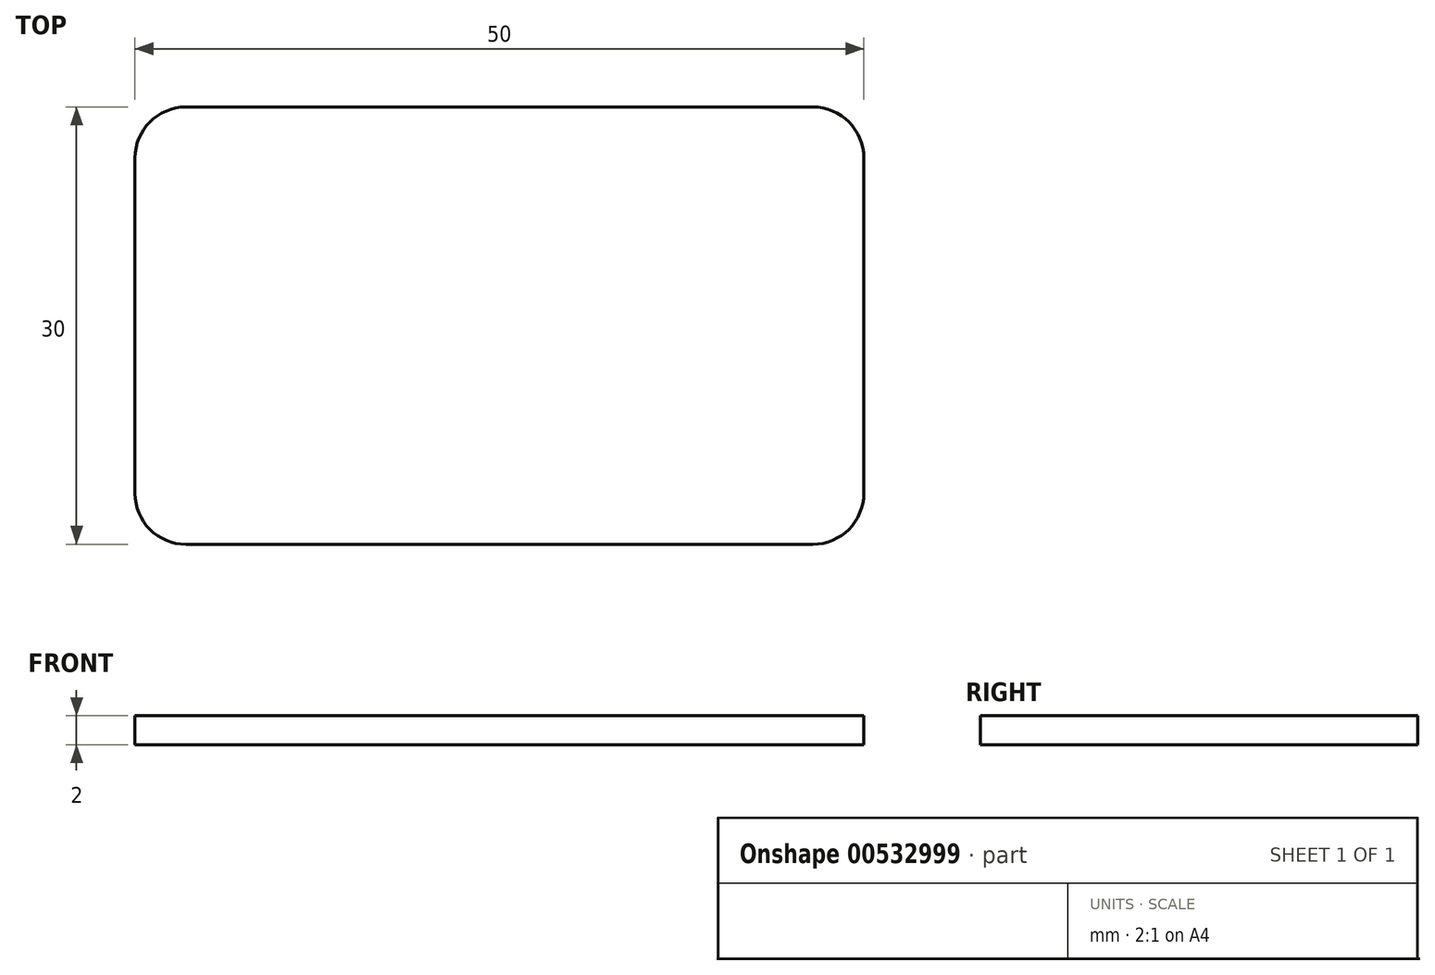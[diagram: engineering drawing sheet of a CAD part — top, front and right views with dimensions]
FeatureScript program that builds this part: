
annotation { "Feature Type Name" : "Feature", "Feature Type Description" : "" }
export const myFeature = defineFeature(function(context is Context, id is Id, definition is map)
    precondition{}
    {
        {
            var Q0;
            Q0=qCreatedBy(makeId("Top.planeOp"),FACE);
            var sketch = newSketch(context, id + "F0", { "sketchPlane" : qUnion([Q0])});
            skLineSegment(sketch, "E0.bottom", {"start": v(21.5, 15) * mm, "end": v(-21.5, 15) * mm});
            skLineSegment(sketch, "E0.top", {"start": v(21.5, -15) * mm, "end": v(-21.5, -15) * mm});
            skLineSegment(sketch, "E0.left", {"start": v(25, 11.5) * mm, "end": v(25, -11.5) * mm});
            skLineSegment(sketch, "E0.right", {"start": v(-25, 11.5) * mm, "end": v(-25, -11.5) * mm});
            skPoint(sketch, "E0.middle", {"position": v(0, 0) * mm});
            skPoint(sketch, "E1.visualSharp", {"position": v(-25, 15) * mm});
            skArc(sketch, "E1.filletArc", {"start": v(-21.5, 15) * mm, "mid": v(-23.97, 13.97) * mm, "end": v(-25, 11.5) * mm});
            skPoint(sketch, "E2.visualSharp", {"position": v(-25, -15) * mm});
            skArc(sketch, "E2.filletArc", {"start": v(-25, -11.5) * mm, "mid": v(-23.97, -13.97) * mm, "end": v(-21.5, -15) * mm});
            skPoint(sketch, "E3.visualSharp", {"position": v(25, -15) * mm});
            skArc(sketch, "E3.filletArc", {"start": v(21.5, -15) * mm, "mid": v(23.97, -13.97) * mm, "end": v(25, -11.5) * mm});
            skPoint(sketch, "E4.visualSharp", {"position": v(25, 15) * mm});
            skArc(sketch, "E4.filletArc", {"start": v(25, 11.5) * mm, "mid": v(23.97, 13.97) * mm, "end": v(21.5, 15) * mm});
            skSolve(sketch);
        }
        {
            var Q0;
            Q0=makeQuery(id+"F0.imprint","IMPRINT",FACE,{"disambiguationData":[TD([[makeQuery(id+"F0.imprint","IMPRINT",EDGE,{"derivedFrom":sQuery(id+"F0.wireOp",EDGE,"E0.bottom")}),1.0]])]});
            extrude(context, id + "F1", {"entities" : qUnion([Q0]), "depth" : 2 * mm, "offsetDistance" : 25 * mm});
        }
    });
